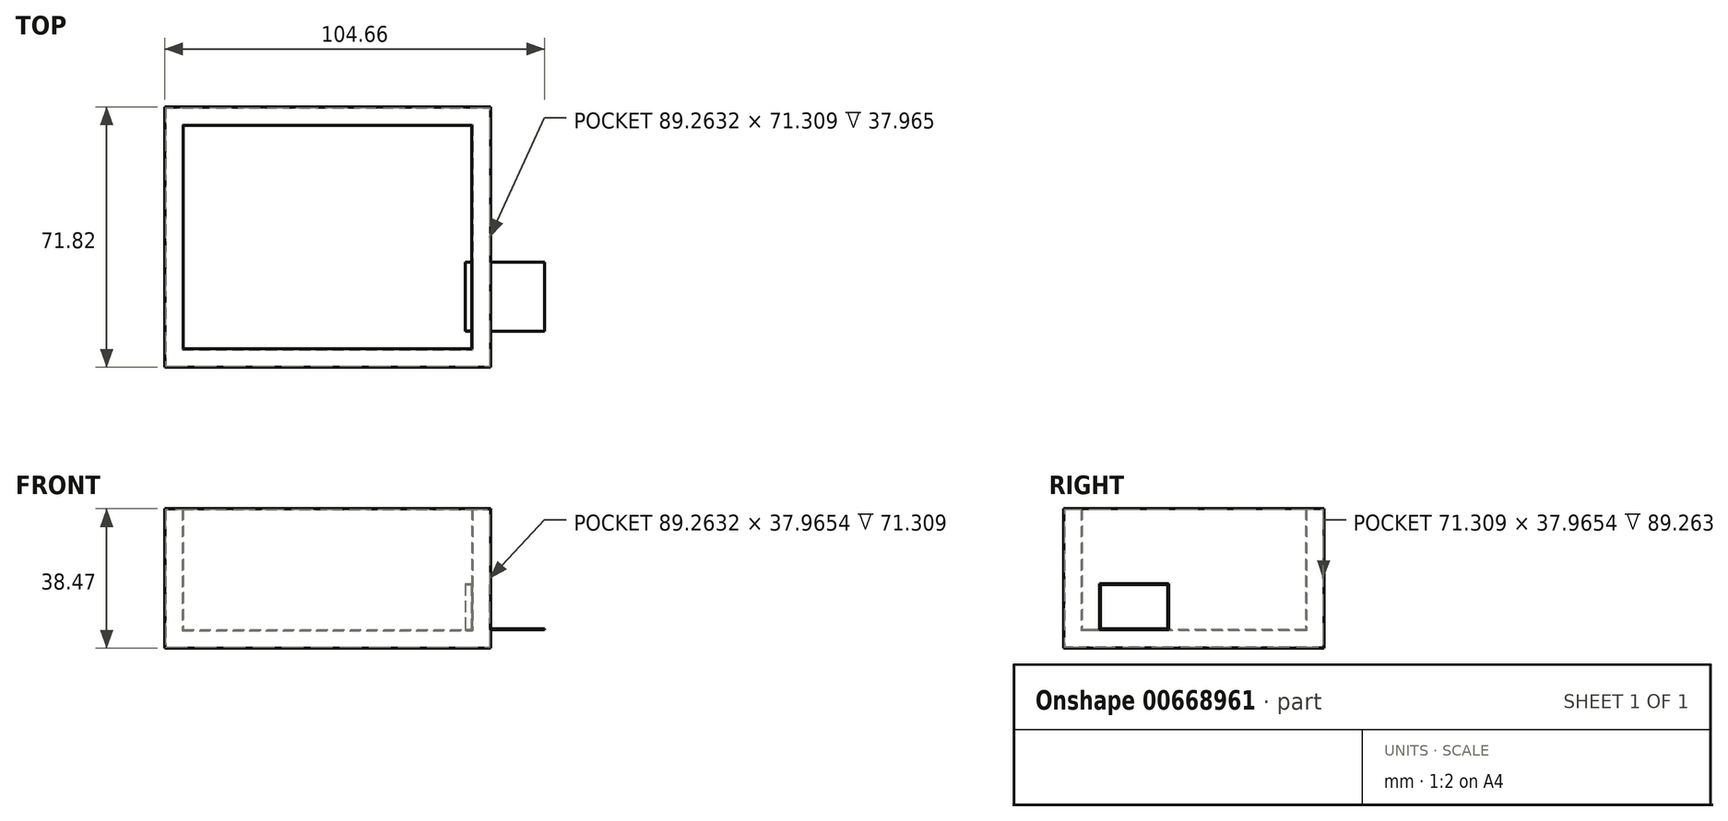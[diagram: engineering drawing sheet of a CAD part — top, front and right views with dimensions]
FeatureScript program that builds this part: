
annotation { "Feature Type Name" : "Feature", "Feature Type Description" : "" }
export const myFeature = defineFeature(function(context is Context, id is Id, definition is map)
    precondition{}
    {
        {
            var Q0;
            Q0=qCreatedBy(makeId("Top.planeOp"),FACE);
            var sketch = newSketch(context, id + "F0", { "sketchPlane" : qUnion([Q0])});
            skLineSegment(sketch, "E0.bottom", {"start": v(-52.86, 6.92) * mm, "end": v(23.34, 6.92) * mm});
            skLineSegment(sketch, "E0.top", {"start": v(-52.86, -51.5) * mm, "end": v(23.34, -51.5) * mm});
            skLineSegment(sketch, "E0.left", {"start": v(-52.86, 6.92) * mm, "end": v(-52.86, -51.5) * mm});
            skLineSegment(sketch, "E0.right", {"start": v(23.34, 6.92) * mm, "end": v(23.34, -51.5) * mm});
            skSolve(sketch);
        }
        {
            var Q0;
            Q0 = qSketchRegion(id + "F0", true);
            extrude(context, id + "F1", {"entities" : qUnion([Q0]), "depth" : 25.4 * mm, "offsetDistance" : 25.4 * mm});
        }
        {
            var Q0;
            Q0 = qSketchRegion(id + "F0", true);
            extrude(context, id + "F2", {"entities" : qUnion([Q0]), "operationType" : NewBodyOperationType.ADD, "depth" : 31.75 * mm, "offsetDistance" : 25.4 * mm});
        }
        {
            var Q0;
            Q0=makeQuery(id+"F1.opExtrude","SWEPT_BODY",BODY,{"disambiguationData":[OSD([sQuery(id+"F0.wireOp",EDGE,"E0.bottom"),sQuery(id+"F0.wireOp",EDGE,"E0.top"),sQuery(id+"F0.wireOp",EDGE,"E0.left"),sQuery(id+"F0.wireOp",EDGE,"E0.right")])]});
            transform(context, id + "F3", {"entities" : qUnion([Q0]), "transformType" : TransformType.TRANSLATION_3D, "dx" : 0 * mm, "dy" : 0 * mm, "dz" : 101.6 * mm, "makeCopy" : true});
        }
        {
            var Q0;
            Q0=makeQuery(id+"F3.opPattern","COPY",FACE,{"derivedFrom":makeQuery(id+"F2.opExtrude","CAP_FACE",FACE,{"disambiguationData":[OSD([sQuery(id+"F0.wireOp",EDGE,"E0.bottom"),sQuery(id+"F0.wireOp",EDGE,"E0.top"),sQuery(id+"F0.wireOp",EDGE,"E0.left"),sQuery(id+"F0.wireOp",EDGE,"E0.right")])],"isStart":false}),"instanceName":"1"});
            extrude(context, id + "F4", {"entities" : qUnion([Q0]), "operationType" : NewBodyOperationType.ADD, "depth" : 6.35 * mm, "offsetDistance" : 25.4 * mm});
        }
        {
            var Q0;
            {var subQ0=sQuery(id+"F0.wireOp",EDGE,"E0.right");Q0=makeQuery(id+"F4.boolean.opBoolean","MERGE",FACE,{"derivedFrom":[makeQuery(id+"F3.opPattern","COPY",FACE,{"derivedFrom":makeQuery(id+"F2.boolean.opBoolean","MERGE",FACE,{"derivedFrom":[makeQuery(id+"F1.opExtrude","SWEPT_FACE",FACE,{"disambiguationData":[OSD([subQ0])]}),makeQuery(id+"F2.opExtrude","SWEPT_FACE",FACE,{"disambiguationData":[OSD([subQ0])]})]}),"instanceName":"1"}),makeQuery(id+"F4.opExtrude","SWEPT_FACE",FACE,{"disambiguationData":[OSD([subQ0])]})]});}
            extrude(context, id + "F5", {"entities" : qUnion([Q0]), "operationType" : NewBodyOperationType.ADD, "depth" : 6.35 * mm, "offsetDistance" : 25.4 * mm});
        }
        {
            var Q0;
            {var subQ0=sQuery(id+"F0.wireOp",EDGE,"E0.left");Q0=makeQuery(id+"F4.boolean.opBoolean","MERGE",FACE,{"derivedFrom":[makeQuery(id+"F3.opPattern","COPY",FACE,{"derivedFrom":makeQuery(id+"F2.boolean.opBoolean","MERGE",FACE,{"derivedFrom":[makeQuery(id+"F1.opExtrude","SWEPT_FACE",FACE,{"disambiguationData":[OSD([subQ0])]}),makeQuery(id+"F2.opExtrude","SWEPT_FACE",FACE,{"disambiguationData":[OSD([subQ0])]})]}),"instanceName":"1"}),makeQuery(id+"F4.opExtrude","SWEPT_FACE",FACE,{"disambiguationData":[OSD([subQ0])]})]});}
            extrude(context, id + "F6", {"entities" : qUnion([Q0]), "operationType" : NewBodyOperationType.ADD, "depth" : 6.35 * mm, "offsetDistance" : 25.4 * mm});
        }
        {
            var Q0;
            {var subQ0=sQuery(id+"F0.wireOp",EDGE,"E0.top");Q0=makeQuery(id+"F6.boolean.opBoolean","MERGE",FACE,{"derivedFrom":[makeQuery(id+"F5.boolean.opBoolean","MERGE",FACE,{"derivedFrom":[makeQuery(id+"F4.boolean.opBoolean","MERGE",FACE,{"derivedFrom":[makeQuery(id+"F3.opPattern","COPY",FACE,{"derivedFrom":makeQuery(id+"F2.boolean.opBoolean","MERGE",FACE,{"derivedFrom":[makeQuery(id+"F1.opExtrude","SWEPT_FACE",FACE,{"disambiguationData":[OSD([subQ0])]}),makeQuery(id+"F2.opExtrude","SWEPT_FACE",FACE,{"disambiguationData":[OSD([subQ0])]})]}),"instanceName":"1"}),makeQuery(id+"F4.opExtrude","SWEPT_FACE",FACE,{"disambiguationData":[OSD([subQ0])]})]}),makeQuery(id+"F5.opExtrude","SWEPT_FACE",FACE,{"disambiguationData":[OSD([subQ0,sQuery(id+"F0.wireOp",EDGE,"E0.right")])]})]}),makeQuery(id+"F6.opExtrude","SWEPT_FACE",FACE,{"disambiguationData":[OSD([subQ0,sQuery(id+"F0.wireOp",EDGE,"E0.left")])]})]});}
            extrude(context, id + "F7", {"entities" : qUnion([Q0]), "operationType" : NewBodyOperationType.ADD, "depth" : 6.35 * mm, "offsetDistance" : 25.4 * mm});
        }
        {
            var Q0;
            {var subQ0=sQuery(id+"F0.wireOp",EDGE,"E0.bottom");Q0=makeQuery(id+"F6.boolean.opBoolean","MERGE",FACE,{"derivedFrom":[makeQuery(id+"F5.boolean.opBoolean","MERGE",FACE,{"derivedFrom":[makeQuery(id+"F4.boolean.opBoolean","MERGE",FACE,{"derivedFrom":[makeQuery(id+"F3.opPattern","COPY",FACE,{"derivedFrom":makeQuery(id+"F2.boolean.opBoolean","MERGE",FACE,{"derivedFrom":[makeQuery(id+"F1.opExtrude","SWEPT_FACE",FACE,{"disambiguationData":[OSD([subQ0])]}),makeQuery(id+"F2.opExtrude","SWEPT_FACE",FACE,{"disambiguationData":[OSD([subQ0])]})]}),"instanceName":"1"}),makeQuery(id+"F4.opExtrude","SWEPT_FACE",FACE,{"disambiguationData":[OSD([subQ0])]})]}),makeQuery(id+"F5.opExtrude","SWEPT_FACE",FACE,{"disambiguationData":[OSD([subQ0,sQuery(id+"F0.wireOp",EDGE,"E0.right")])]})]}),makeQuery(id+"F6.opExtrude","SWEPT_FACE",FACE,{"disambiguationData":[OSD([subQ0,sQuery(id+"F0.wireOp",EDGE,"E0.left")])]})]});}
            extrude(context, id + "F8", {"entities" : qUnion([Q0]), "operationType" : NewBodyOperationType.ADD, "depth" : 6.35 * mm, "offsetDistance" : 25.4 * mm});
        }
        {
            var Q0;
            {var subQ0=sQuery(id+"F0.wireOp",EDGE,"E0.left");var subQ1=sQuery(id+"F0.wireOp",EDGE,"E0.bottom");var subQ2=sQuery(id+"F0.wireOp",EDGE,"E0.right");var subQ3=sQuery(id+"F0.wireOp",EDGE,"E0.top");Q0=makeQuery(id+"F8.boolean.opBoolean","MERGE",FACE,{"derivedFrom":[makeQuery(id+"F7.boolean.opBoolean","MERGE",FACE,{"derivedFrom":[makeQuery(id+"F6.boolean.opBoolean","MERGE",FACE,{"derivedFrom":[makeQuery(id+"F5.boolean.opBoolean","MERGE",FACE,{"derivedFrom":[makeQuery(id+"F4.opExtrude","CAP_FACE",FACE,{"disambiguationData":[OSD([subQ1,subQ3,subQ0,subQ2])],"isStart":false}),makeQuery(id+"F5.opExtrude","SWEPT_FACE",FACE,{"disambiguationData":[OSD([subQ2]),TDD([makeQuery(id+"F4.opExtrude","CAP_EDGE",EDGE,{"disambiguationData":[OSD([subQ2])],"isStart":false})])]})]}),makeQuery(id+"F6.opExtrude","SWEPT_FACE",FACE,{"disambiguationData":[OSD([subQ0]),TDD([makeQuery(id+"F4.opExtrude","CAP_EDGE",EDGE,{"disambiguationData":[OSD([subQ0])],"isStart":false})])]})]}),makeQuery(id+"F7.opExtrude","SWEPT_FACE",FACE,{"disambiguationData":[OSD([subQ3,subQ0,subQ2]),TDD([makeQuery(id+"F6.boolean.opBoolean","MERGE",EDGE,{"derivedFrom":[makeQuery(id+"F5.boolean.opBoolean","MERGE",EDGE,{"derivedFrom":[makeQuery(id+"F4.opExtrude","CAP_EDGE",EDGE,{"disambiguationData":[OSD([subQ3])],"isStart":false}),makeQuery(id+"F5.opExtrude","SWEPT_EDGE",EDGE,{"disambiguationData":[OSD([subQ3,subQ2]),TDD([makeQuery(id+"F4.opExtrude","CAP_VERTEX",VERTEX,{"disambiguationData":[OSD([subQ3,subQ2])],"isStart":false})])]})]}),makeQuery(id+"F6.opExtrude","SWEPT_EDGE",EDGE,{"disambiguationData":[OSD([subQ3,subQ0]),TDD([makeQuery(id+"F4.opExtrude","CAP_VERTEX",VERTEX,{"disambiguationData":[OSD([subQ3,subQ0])],"isStart":false})])]})]})])]})]}),makeQuery(id+"F8.opExtrude","SWEPT_FACE",FACE,{"disambiguationData":[OSD([subQ1,subQ0,subQ2]),TDD([makeQuery(id+"F6.boolean.opBoolean","MERGE",EDGE,{"derivedFrom":[makeQuery(id+"F5.boolean.opBoolean","MERGE",EDGE,{"derivedFrom":[makeQuery(id+"F4.opExtrude","CAP_EDGE",EDGE,{"disambiguationData":[OSD([subQ1])],"isStart":false}),makeQuery(id+"F5.opExtrude","SWEPT_EDGE",EDGE,{"disambiguationData":[OSD([subQ1,subQ2]),TDD([makeQuery(id+"F4.opExtrude","CAP_VERTEX",VERTEX,{"disambiguationData":[OSD([subQ1,subQ2])],"isStart":false})])]})]}),makeQuery(id+"F6.opExtrude","SWEPT_EDGE",EDGE,{"disambiguationData":[OSD([subQ1,subQ0]),TDD([makeQuery(id+"F4.opExtrude","CAP_VERTEX",VERTEX,{"disambiguationData":[OSD([subQ1,subQ0])],"isStart":false})])]})]})])]})]});}
            shell(context, id + "F9", {"entities" : qUnion([Q0]), "thickness" : 5.08 * mm});
        }
        {
            var Q0;
            Q0=makeQuery(id+"F3.opPattern","COPY",BODY,{"derivedFrom":makeQuery(id+"F1.opExtrude","SWEPT_BODY",BODY,{"disambiguationData":[OSD([sQuery(id+"F0.wireOp",EDGE,"E0.bottom"),sQuery(id+"F0.wireOp",EDGE,"E0.top"),sQuery(id+"F0.wireOp",EDGE,"E0.left"),sQuery(id+"F0.wireOp",EDGE,"E0.right")])]}),"instanceName":"1"});
            transform(context, id + "F10", {"entities" : qUnion([Q0]), "transformType" : TransformType.TRANSLATION_3D, "dx" : 0 * mm, "dy" : 0 * mm, "dz" : -101.6 * mm, "makeCopy" : false});
        }
        {
            var Q0;
            Q0=makeQuery(id+"F1.opExtrude","SWEPT_BODY",BODY,{"disambiguationData":[OSD([sQuery(id+"F0.wireOp",EDGE,"E0.bottom"),sQuery(id+"F0.wireOp",EDGE,"E0.top"),sQuery(id+"F0.wireOp",EDGE,"E0.left"),sQuery(id+"F0.wireOp",EDGE,"E0.right")])]});
            deleteBodies(context, id + "F11", {"entities" : qUnion([Q0])});
        }
        {
            var Q0;
            Q0=makeQuery(id+"F3.opPattern","COPY",BODY,{"derivedFrom":makeQuery(id+"F1.opExtrude","SWEPT_BODY",BODY,{"disambiguationData":[OSD([sQuery(id+"F0.wireOp",EDGE,"E0.bottom"),sQuery(id+"F0.wireOp",EDGE,"E0.top"),sQuery(id+"F0.wireOp",EDGE,"E0.left"),sQuery(id+"F0.wireOp",EDGE,"E0.right")])]}),"instanceName":"1"});
            var Q1;
            Q1=qCreatedBy(makeId("Origin.pointOp"),VERTEX);
            transform(context, id + "F12", {"entities" : qUnion([Q0]), "transformType" : TransformType.SCALE_UNIFORMLY, "scale" : 0.9, "scalePoint" : qUnion([Q1]), "makeCopy" : false});
        }
        {
            var Q0;
            Q0=makeQuery(id+"F3.opPattern","COPY",BODY,{"derivedFrom":makeQuery(id+"F1.opExtrude","SWEPT_BODY",BODY,{"disambiguationData":[OSD([sQuery(id+"F0.wireOp",EDGE,"E0.bottom"),sQuery(id+"F0.wireOp",EDGE,"E0.top"),sQuery(id+"F0.wireOp",EDGE,"E0.left"),sQuery(id+"F0.wireOp",EDGE,"E0.right")])]}),"instanceName":"1"});
            var Q1;
            Q1=qCreatedBy(makeId("Origin.pointOp"),VERTEX);
            transform(context, id + "F13", {"entities" : qUnion([Q0]), "transformType" : TransformType.SCALE_UNIFORMLY, "scale" : 1.02, "scalePoint" : qUnion([Q1]), "makeCopy" : false});
        }
        {
            var Q0;
            Q0=makeQuery(id+"F3.opPattern","COPY",BODY,{"derivedFrom":makeQuery(id+"F1.opExtrude","SWEPT_BODY",BODY,{"disambiguationData":[OSD([sQuery(id+"F0.wireOp",EDGE,"E0.bottom"),sQuery(id+"F0.wireOp",EDGE,"E0.top"),sQuery(id+"F0.wireOp",EDGE,"E0.left"),sQuery(id+"F0.wireOp",EDGE,"E0.right")])]}),"instanceName":"1"});
            var Q1;
            Q1=qCreatedBy(makeId("Origin.pointOp"),VERTEX);
            transform(context, id + "F14", {"entities" : qUnion([Q0]), "transformType" : TransformType.SCALE_UNIFORMLY, "scale" : 1.1, "scalePoint" : qUnion([Q1]), "makeCopy" : false});
        }
        {
            var Q0;
            {var subQ0=sQuery(id+"F0.wireOp",EDGE,"E0.left");Q0=makeQuery(id+"F8.boolean.opBoolean","MERGE",FACE,{"derivedFrom":[makeQuery(id+"F7.boolean.opBoolean","MERGE",FACE,{"derivedFrom":[makeQuery(id+"F6.opExtrude","CAP_FACE",FACE,{"disambiguationData":[OSD([subQ0])],"isStart":false}),makeQuery(id+"F7.opExtrude","SWEPT_FACE",FACE,{"disambiguationData":[OSD([sQuery(id+"F0.wireOp",EDGE,"E0.top"),subQ0])]})]}),makeQuery(id+"F8.opExtrude","SWEPT_FACE",FACE,{"disambiguationData":[OSD([sQuery(id+"F0.wireOp",EDGE,"E0.bottom"),subQ0])]})]});}
            var sketch = newSketch(context, id + "F15", { "sketchPlane" : qUnion([Q0])});
            skPoint(sketch, "E1.firstSnap0", {"position": v(-13.4, 19.24) * mm});
            skLineSegment(sketch, "E1.bottom", {"start": v(-4.36, 19.24) * mm, "end": v(8.57, 19.24) * mm});
            skLineSegment(sketch, "E1.top", {"start": v(-4.36, 12.73) * mm, "end": v(8.57, 12.73) * mm});
            skLineSegment(sketch, "E1.left", {"start": v(-4.36, 19.24) * mm, "end": v(-4.36, 12.73) * mm});
            skLineSegment(sketch, "E1.right", {"start": v(8.57, 19.24) * mm, "end": v(8.57, 12.73) * mm});
            skSolve(sketch);
        }
        {
            var Q0;
            Q0=makeQuery(id+"F15.imprint","IMPRINT",FACE,{"disambiguationData":[TD([[makeQuery(id+"F15.imprint","IMPRINT",EDGE,{"derivedFrom":sQuery(id+"F15.wireOp",EDGE,"E1.bottom")}),-1.0]])]});
            extrude(context, id + "F16", {"entities" : qUnion([Q0]), "operationType" : NewBodyOperationType.ADD, "oppositeDirection" : true, "depth" : 5.08 * mm, "offsetDistance" : 25.4 * mm});
        }
        {
            var Q0;
            Q0=qCreatedBy(makeId("Top.planeOp"),FACE);
            cPlane(context, id + "F17", {"entities" : qUnion([Q0]), "cplaneType" : CPlaneType.OFFSET, "offset" : 5.08 * mm, "width" : 152.4 * mm, "height" : 152.4 * mm});
        }
        {
            var Q0;
            Q0=qCreatedBy(id+"F17.planeOp",FACE);
            var sketch = newSketch(context, id + "F18", { "sketchPlane" : qUnion([Q0])});
            skLineSegment(sketch, "E2.bottom", {"start": v(22.96, -48.54) * mm, "end": v(44.87, -48.54) * mm});
            skLineSegment(sketch, "E2.top", {"start": v(22.96, -29.49) * mm, "end": v(44.87, -29.49) * mm});
            skLineSegment(sketch, "E2.left", {"start": v(22.96, -48.54) * mm, "end": v(22.96, -29.49) * mm});
            skLineSegment(sketch, "E2.right", {"start": v(44.87, -48.54) * mm, "end": v(44.87, -29.49) * mm});
            skSolve(sketch);
        }
        {
            var Q0;
            Q0=makeQuery(id+"F18.imprint","IMPRINT",FACE,{"disambiguationData":[TD([[makeQuery(id+"F18.imprint","IMPRINT",EDGE,{"derivedFrom":sQuery(id+"F18.wireOp",EDGE,"E2.bottom")}),1.0]])]});
            var Q1;
            Q1 = qSketchRegion(id + "F18", true);
            extrude(context, id + "F19", {"entities" : qUnion([Q0, Q1]), "operationType" : NewBodyOperationType.ADD, "depth" : 12.7 * mm, "offsetDistance" : 25.4 * mm});
        }
        {
            var Q0;
            Q0=makeQuery(id+"F19.opExtrude","SWEPT_FACE",FACE,{"disambiguationData":[OSD([sQuery(id+"F18.wireOp",EDGE,"E2.left")])]});
            var Q1;
            {var subQ0=sQuery(id+"F0.wireOp",EDGE,"E0.right");var subQ4=sQuery(id+"F18.wireOp",EDGE,"E2.bottom");Q1=makeQuery(id+"F19.boolean.opBoolean","SPLIT",FACE,{"disambiguationData":[TD([makeQuery(id+"F5.opExtrude","CAP_FACE",FACE,{"disambiguationData":[OSD([subQ0])],"isStart":false})])],"derivedFrom":makeQuery(id+"F19.opExtrude","SWEPT_FACE",FACE,{"disambiguationData":[OSD([subQ4])]})});}
            var Q2;
            {var subQ0=sQuery(id+"F0.wireOp",EDGE,"E0.right");var subQ3=sQuery(id+"F18.wireOp",EDGE,"E2.top");Q2=makeQuery(id+"F19.boolean.opBoolean","SPLIT",FACE,{"disambiguationData":[TD([makeQuery(id+"F5.opExtrude","CAP_FACE",FACE,{"disambiguationData":[OSD([subQ0])],"isStart":false})])],"derivedFrom":makeQuery(id+"F19.opExtrude","SWEPT_FACE",FACE,{"disambiguationData":[OSD([subQ3])]})});}
            var Q3;
            {var subQ0=sQuery(id+"F18.wireOp",EDGE,"E2.bottom");var subQ1=sQuery(id+"F0.wireOp",EDGE,"E0.right");var subQ2=sQuery(id+"F18.wireOp",EDGE,"E2.top");var subQ3=sQuery(id+"F18.wireOp",EDGE,"E2.right");Q3=makeQuery(id+"F19.boolean.opBoolean","SPLIT",FACE,{"disambiguationData":[TD([makeQuery(id+"F5.opExtrude","CAP_FACE",FACE,{"disambiguationData":[OSD([subQ1])],"isStart":false})])],"derivedFrom":makeQuery(id+"F19.opExtrude","CAP_FACE",FACE,{"disambiguationData":[OSD([subQ0,subQ2,sQuery(id+"F18.wireOp",EDGE,"E2.left"),subQ3])],"isStart":false})});}
            var Q4;
            Q4=makeQuery(id+"F19.opExtrude","SWEPT_FACE",FACE,{"disambiguationData":[OSD([sQuery(id+"F18.wireOp",EDGE,"E2.right")])]});
            shell(context, id + "F20", {"entities" : qUnion([Q0, Q1, Q2, Q3, Q4]), "thickness" : 0.25 * mm});
        }
    });
